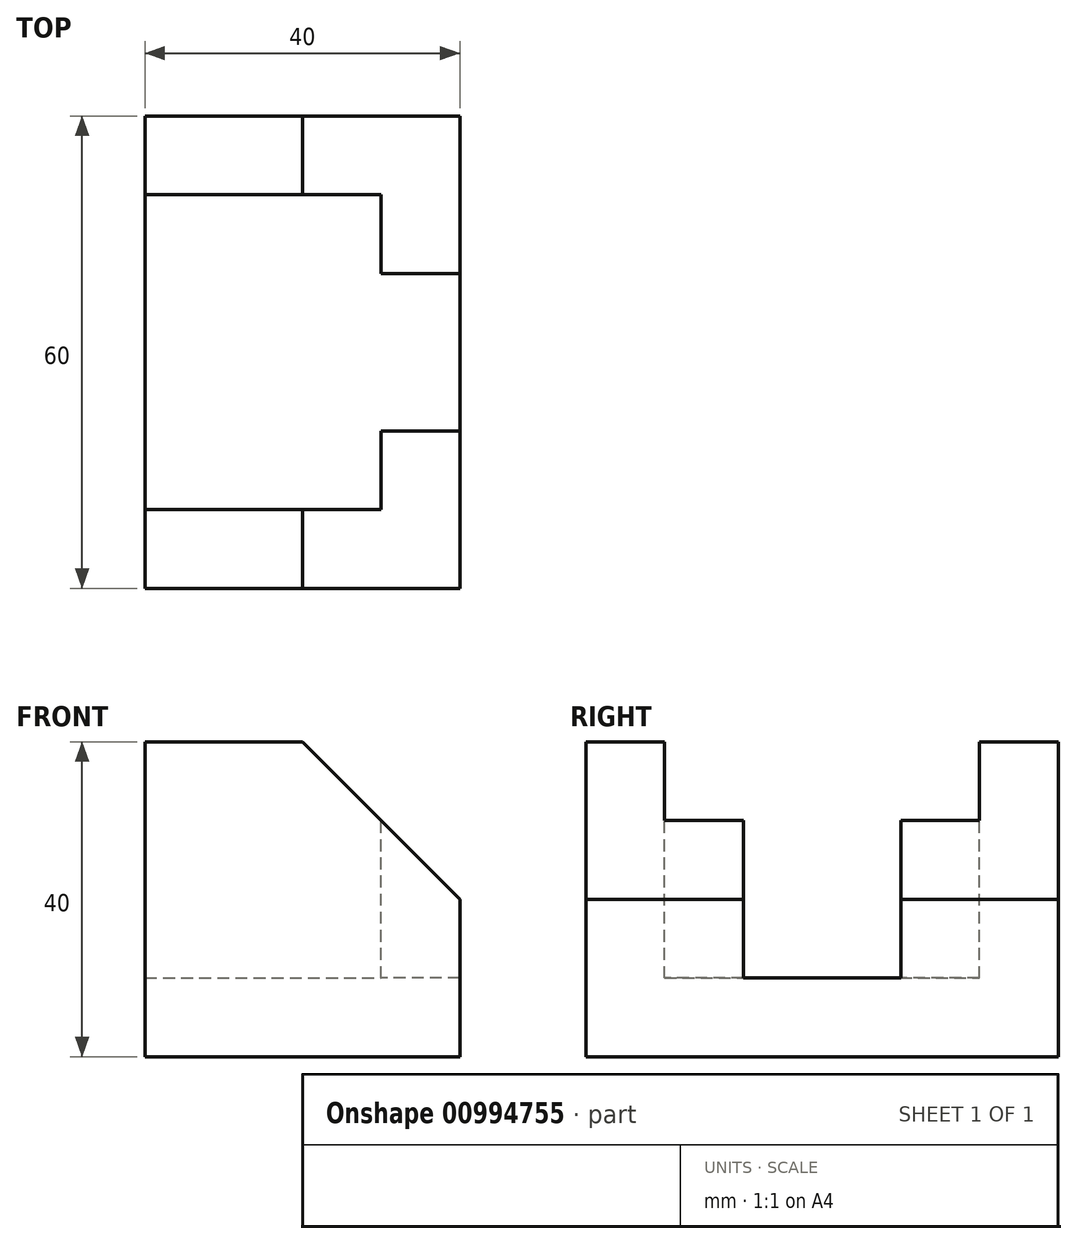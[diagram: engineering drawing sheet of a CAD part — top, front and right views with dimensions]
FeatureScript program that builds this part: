
annotation { "Feature Type Name" : "Feature", "Feature Type Description" : "" }
export const myFeature = defineFeature(function(context is Context, id is Id, definition is map)
    precondition{}
    {
        {
            var Q0;
            Q0=qCreatedBy(makeId("Front.planeOp"),FACE);
            var sketch = newSketch(context, id + "F0", { "sketchPlane" : qUnion([Q0])});
            skLineSegment(sketch, "E0.bottom", {"start": v(-20, 40) * mm, "end": v(0, 40) * mm});
            skLineSegment(sketch, "E0.top", {"start": v(-20, 0) * mm, "end": v(20, 0) * mm});
            skLineSegment(sketch, "E0.left", {"start": v(-20, 40) * mm, "end": v(-20, 0) * mm});
            skLineSegment(sketch, "E0.right", {"start": v(20, 20) * mm, "end": v(20, 0) * mm});
            skLineSegment(sketch, "E1", {"start": v(0, 40) * mm, "end": v(20, 20) * mm});
            skSolve(sketch);
        }
        {
            var Q0;
            Q0 = qSketchRegion(id + "F0", true);
            extrude(context, id + "F1", {"entities" : qUnion([Q0]), "endBound" : BoundingType.SYMMETRIC, "depth" : 60 * mm, "offsetDistance" : 25 * mm});
        }
        {
            var Q0;
            Q0=makeQuery(id+"F1.opExtrude","SWEPT_FACE",FACE,{"disambiguationData":[OSD([sQuery(id+"F0.wireOp",EDGE,"E0.bottom")])]});
            var sketch = newSketch(context, id + "F2", { "sketchPlane" : qUnion([Q0])});
            skLineSegment(sketch, "E2", {"start": v(-20, 20) * mm, "end": v(10, 20) * mm});
            skLineSegment(sketch, "E3", {"start": v(10, 20) * mm, "end": v(10, 10) * mm});
            skLineSegment(sketch, "E4", {"start": v(10, 10) * mm, "end": v(20, 10) * mm});
            skLineSegment(sketch, "E5", {"start": v(20, 10) * mm, "end": v(20, -10) * mm});
            skLineSegment(sketch, "E6", {"start": v(20, -10) * mm, "end": v(10, -10) * mm});
            skLineSegment(sketch, "E7", {"start": v(10, -10) * mm, "end": v(10, -20) * mm});
            skLineSegment(sketch, "E8", {"start": v(10, -20) * mm, "end": v(-20, -20) * mm});
            skLineSegment(sketch, "E9", {"start": v(-20, -20) * mm, "end": v(-20, 20) * mm});
            skSolve(sketch);
        }
        {
            var Q0;
            {var subQ0=sQuery(id+"F2.wireOp",EDGE,"E3");Q0=makeQuery(id+"F2.imprint","IMPRINT",FACE,{"disambiguationData":[TD([[makeQuery(id+"F2.imprint","IMPRINT",EDGE,{"derivedFrom":subQ0}),-1.0]])]});}
            var Q1;
            {var subQ0=sQuery(id+"F2.wireOp",EDGE,"E9");Q1=makeQuery(id+"F2.imprint","IMPRINT",FACE,{"disambiguationData":[TD([[makeQuery(id+"F2.imprint","IMPRINT",EDGE,{"derivedFrom":subQ0}),-1.0]])]});}
            extrude(context, id + "F3", {"entities" : qUnion([Q0, Q1]), "operationType" : NewBodyOperationType.REMOVE, "oppositeDirection" : true, "depth" : 30 * mm, "offsetDistance" : 25 * mm});
        }
    });
